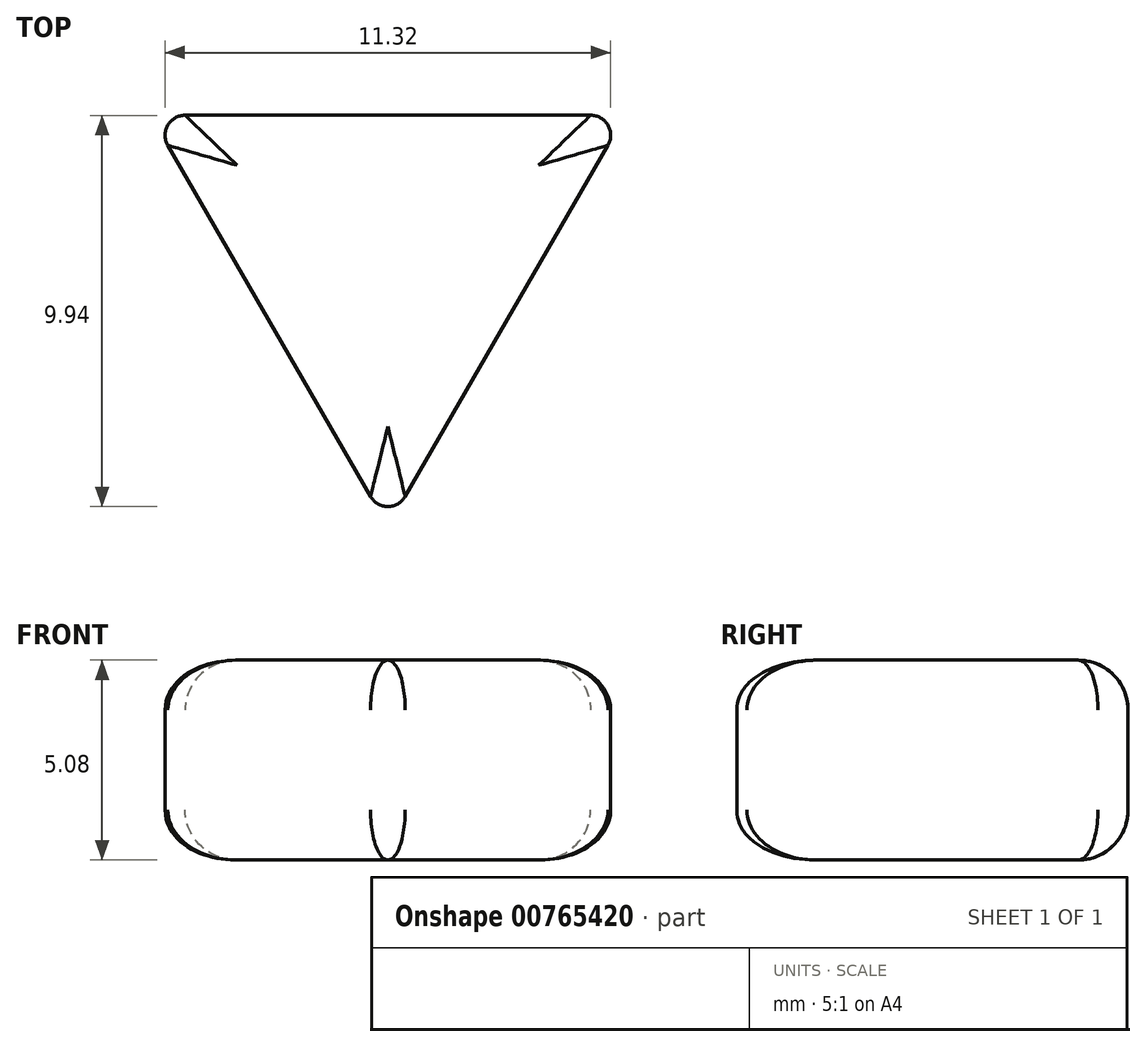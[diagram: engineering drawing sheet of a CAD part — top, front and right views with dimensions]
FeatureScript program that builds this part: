
annotation { "Feature Type Name" : "Feature", "Feature Type Description" : "" }
export const myFeature = defineFeature(function(context is Context, id is Id, definition is map)
    precondition{}
    {
        {
            var Q0;
            Q0=qCreatedBy(makeId("Top.planeOp"),FACE);
            var sketch = newSketch(context, id + "F0", { "sketchPlane" : qUnion([Q0])});
            skPoint(sketch, "E0", {"position": v(0, 0) * mm});
            skLineSegment(sketch, "E1.bottom", {"start": v(5.15, 5.22) * mm, "end": v(-5.15, 5.22) * mm});
            skLineSegment(sketch, "E2", {"start": v(-5.6, 4.46) * mm, "end": v(-0.44, -4.46) * mm});
            skLineSegment(sketch, "E3", {"start": v(0.44, -4.46) * mm, "end": v(5.6, 4.46) * mm});
            skPoint(sketch, "E4", {"position": v(0, 5.22) * mm});
            skPoint(sketch, "E5.visualSharp", {"position": v(0, -5.22) * mm});
            skArc(sketch, "E5.filletArc", {"start": v(-0.44, -4.46) * mm, "mid": v(0, -4.72) * mm, "end": v(0.44, -4.46) * mm});
            skPoint(sketch, "E6.visualSharp", {"position": v(-6.03, 5.22) * mm});
            skArc(sketch, "E6.filletArc", {"start": v(-5.15, 5.22) * mm, "mid": v(-5.6, 4.97) * mm, "end": v(-5.6, 4.46) * mm});
            skPoint(sketch, "E7.visualSharp", {"position": v(6.03, 5.22) * mm});
            skArc(sketch, "E7.filletArc", {"start": v(5.6, 4.46) * mm, "mid": v(5.6, 4.97) * mm, "end": v(5.15, 5.22) * mm});
            skSolve(sketch);
        }
        {
            var Q0;
            Q0=makeQuery(id+"F0.imprint","IMPRINT",FACE,{"disambiguationData":[TD([[makeQuery(id+"F0.imprint","IMPRINT",EDGE,{"derivedFrom":sQuery(id+"F0.wireOp",EDGE,"E1.bottom")}),1.0]])]});
            extrude(context, id + "F1", {"entities" : qUnion([Q0]), "depth" : 5.08 * mm, "offsetDistance" : 25.4 * mm});
        }
        {
            var Q0;
            Q0=makeQuery(id+"F1.opExtrude","CAP_EDGE",EDGE,{"disambiguationData":[OSD([sQuery(id+"F0.wireOp",EDGE,"E3")])],"isStart":false});
            var Q1;
            Q1=makeQuery(id+"F1.opExtrude","CAP_EDGE",EDGE,{"disambiguationData":[OSD([sQuery(id+"F0.wireOp",EDGE,"E3")])],"isStart":true});
            fillet(context, id + "F2", {"entities" : qUnion([Q0, Q1]), "radius" : 1.27 * mm, "tangentPropagation" : true, "allowEdgeOverflow" : false});
        }
    });
